# Revit family: VRWB-3551
name_source: partatom
category: Lighting Fixtures
units: mm (PartAtom-declared; Revit-internal decimal feet)

## family parameters
Always vertical = Yes
Cut with Voids When Loaded = No
Host = Wall
Light Source = Yes
OmniClass Number = 23.80.70.00
OmniClass Title = Lighting
Part Type = Normal
Room Calculation Point = No
Round Connector Dimension = Use Diameter
Shared = No

## types (4) — shared parameters
Assembly Code = D5020200
Color Filter = 16777215
Description = LED Vandal Resistant Wall Mount - Bullnose Style
Dimming Lamp Color Temperature Shift = <None>
Housing Finish = Metal - Viscor - White
Lamp = LED
Lens Finish = Polycarbonate - Viscor - Clear
Manufacturer = CERTOLUX by VISCOR
Model = VRWB-3551
Tilt Angle = -180.00°
URL = https://www.viscor.com
Voltage = 120 V
Width = 0' - 10 1/2"

## per-type parameters (varying)
| type | Apparent Load | Emit from Line Length | Lamp Wattage | Length | Photometric Web File |
| VRWB-3551-1X4-LED840K52L-P08P82 | 44 VA | 4' - 2 21/32" | 44 VA | 4' - 2 21/32" | VRWB-3551-1X4-LED840K52L-P08P82.ies |
| VRWB-3551-1X4-LED840K78L-P08P82 | 66 VA | 4' - 2 21/32" | 66 VA | 4' - 2 21/32" | VRWB-3551-1X4-LED840K78L-P08P82.ies |
| VRWB-3551-1X4-LED840K104L-P08P82 | 102 VA | 4' - 2 21/32" | 102 VA | 4' - 2 21/32" | VRWB-3551-1X4-LED840K104L-P08P82.ies |
| VRWB-3551-1X2-LED840K52L-P08P82 | 44 VA | 2' - 2 19/32" | 44 VA | 2' - 2 19/32" | VRWB-3551-1X2-LED840K52L-P08P82.ies |

## geometry (parser evidence)
native form markers: Sweep x2
no freeform markers — native parametric forms only
